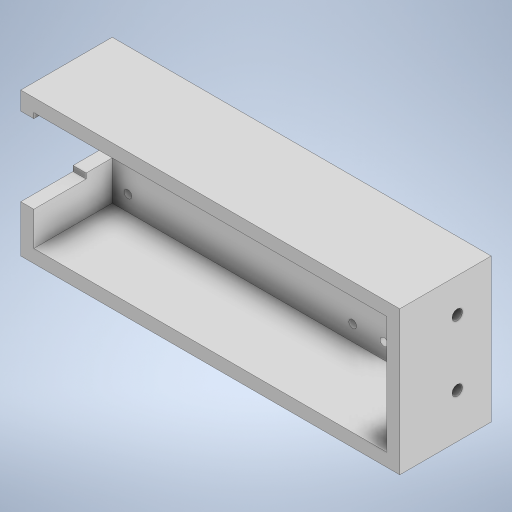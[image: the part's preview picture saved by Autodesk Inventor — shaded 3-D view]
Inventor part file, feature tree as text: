
AUTODESK INVENTOR PART (.ipt)
format: ipt  version: 2023 (Build 270158000, 158)  size: 277,504 bytes
history: native  units: mm
features: extrude x5, sketch x5
ambient origin geometry x8: Origin, YZ Plane, XZ Plane, XY Plane, X Axis, Y Axis, Z Axis, Center Point
bodies: Solid1 (feature_tree)
feature tree (10):
  extrude  "Extrusion1"  Depth=145.0mm
  extrude  "Extrusion2"  Depth=5.0mm
  extrude  "Extrusion3"  Depth=5.0mm
  extrude  "Extrusion4"  Depth=30.0mm TaperAngle=0.0deg
  extrude  "Extrusion5"  Depth=30.0mm
  sketch  "Sketch1"  dims[d0=55.0mm d1=145.0mm]
  sketch  "Sketch2"  dims[d2=35.0mm d3=0.0mm d4=5.0mm]
  sketch  "Sketch3"  dims[d5=5.0mm d6=5.0mm]
  sketch  "Sketch4"  dims[d7=5.0mm d8=30.0mm d9=0.0mm]
  sketch  "Sketch5"  dims[d10=3.0mm d11=11.0mm d12=11.0mm d13=11.0mm d14=11.0mm d15=3.0mm d19=3.0mm d20=3.0mm d24=36.0mm d26=12.0mm d27=36.0mm d28=12.0mm d29=3.0mm d30=3.0mm d31=11.0mm d32=11.0mm d33=11.0mm d34=11.0mm d35=30.0mm d36=0.0mm d37=7.0mm d38=30.0mm d42=30.0mm d43=0.0mm d44=10.0mm d45=25.0mm d46=5.0mm d47=15.0mm d48=4.0mm d49=4.0mm d50=25.0mm d51=13.0mm d52=13.0mm d53=17.0mm d54=30.0mm d55=0.0mm]
